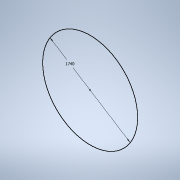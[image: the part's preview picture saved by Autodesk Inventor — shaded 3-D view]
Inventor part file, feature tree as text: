
AUTODESK INVENTOR PART (.ipt)
format: ipt  version: 2021 (Build 250183000, 183)  size: 164,352 bytes
history: native  units: mm
features: other x48, sketch x4, pattern_circular x2, extrude x2, mirror x1
ambient origin geometry x8: Origin, YZ Plane, XZ Plane, XY Plane, X Axis, Y Axis, Z Axis, Center Point
bodies: Body1 (feature_tree), Body2 (feature_tree)
feature tree (57):
  other  "Bryła1"
  sketch  "Szkic1"
  other  "Płaszczyzna konstrukcyjna1"
  other  "Pogrubienie1"
  other  "Punkt konstrukcyjny1"
  other  "Rozdarcie1"
  other  "Punkt konstrukcyjny2"
  other  "Rozdarcie2"
  other  "Punkt konstrukcyjny3"
  pattern_circular  "Szyk kołowy1"  Count=174  [1 undecoded]
  other  "Płaszczyzna konstrukcyjna2"
  mirror  "Odbij1"
  other  "Płaszczyzna konstrukcyjna4"
  sketch  "Szkic3"
  pattern_circular  "Szyk kołowy2"  Count=100  [1 undecoded]
  extrude  "Wyciągnięcie proste1"  Depth=1740.0mm
  extrude  "Wyciągnięcie proste2"  TaperAngle=0.0deg  [1 undecoded]
  sketch  "Szkic2"
  other  "Srf1"
  other  "Punkt konstrukcyjny4"
  other  "Punkt konstrukcyjny5"
  other  "Punkt konstrukcyjny6"
  other  "Punkt konstrukcyjny7"
  other  "Punkt konstrukcyjny8"
  other  "Punkt konstrukcyjny9"
  other  "Punkt konstrukcyjny10"
  other  "Punkt konstrukcyjny11"
  other  "Punkt konstrukcyjny12"
  other  "Punkt konstrukcyjny13"
  other  "Punkt konstrukcyjny14"
  other  "Punkt konstrukcyjny15"
  other  "Punkt konstrukcyjny16"
  other  "Punkt konstrukcyjny17"
  other  "Punkt konstrukcyjny18"
  other  "Punkt konstrukcyjny19"
  other  "Punkt konstrukcyjny20"
  other  "Punkt konstrukcyjny21"
  other  "Punkt konstrukcyjny22"
  other  "Punkt konstrukcyjny23"
  other  "Punkt konstrukcyjny24"
  other  "Punkt konstrukcyjny25"
  other  "Punkt konstrukcyjny26"
  other  "Punkt konstrukcyjny27"
  other  "Punkt konstrukcyjny28"
  other  "Punkt konstrukcyjny29"
  other  "Punkt konstrukcyjny30"
  other  "Punkt konstrukcyjny31"
  other  "Punkt konstrukcyjny32"
  other  "Punkt konstrukcyjny33"
  other  "Punkt konstrukcyjny34"
  other  "Punkt konstrukcyjny35"
  other  "Punkt konstrukcyjny36"
  other  "Punkt konstrukcyjny37"
  other  "Punkt konstrukcyjny38"
  other  "Płaszczyzna konstrukcyjna5"
  sketch  "Szkic4"
  other  "PowWyciągnięciaZłożonego1"
note: 3 required parameter values undecoded (feature->parameter linkage not recoverable at this tier; creation-order binding heuristic only, values carry confidence <= 0.55)
